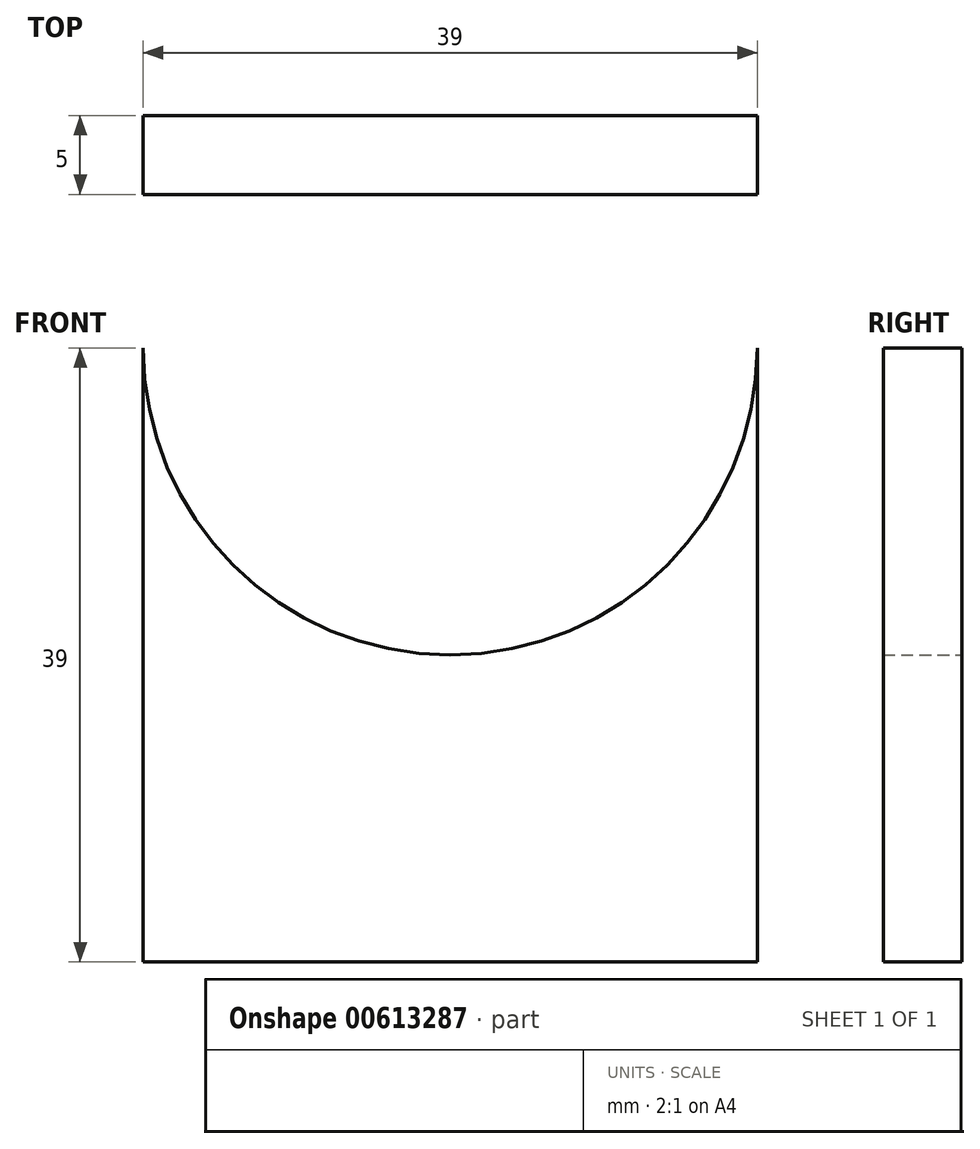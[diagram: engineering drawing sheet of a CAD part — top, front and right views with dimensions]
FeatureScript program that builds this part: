
annotation { "Feature Type Name" : "Feature", "Feature Type Description" : "" }
export const myFeature = defineFeature(function(context is Context, id is Id, definition is map)
    precondition{}
    {
        {
            var Q0;
            Q0=qCreatedBy(makeId("Front.planeOp"),FACE);
            var sketch = newSketch(context, id + "F0", { "sketchPlane" : qUnion([Q0])});
            skLineSegment(sketch, "E0.bottom", {"start": v(-13.94, 0) * mm, "end": v(25.06, 0) * mm});
            skLineSegment(sketch, "E0.top", {"start": v(-13.94, -39) * mm, "end": v(25.06, -39) * mm});
            skLineSegment(sketch, "E0.left", {"start": v(-13.94, 0) * mm, "end": v(-13.94, -39) * mm});
            skLineSegment(sketch, "E0.right", {"start": v(25.06, 0) * mm, "end": v(25.06, -39) * mm});
            skCircle(sketch, "E1", {"center": v(5.56, 0) * mm, "radius": 19.5 * mm});
            skLineSegment(sketch, "E2.bottom", {"start": v(25.06, -28.52) * mm, "end": v(-13.94, -28.52) * mm});
            skLineSegment(sketch, "E2.top", {"start": v(25.06, -39) * mm, "end": v(-13.94, -39) * mm});
            skLineSegment(sketch, "E2.left", {"start": v(25.06, -28.52) * mm, "end": v(25.06, -39) * mm});
            skLineSegment(sketch, "E2.right", {"start": v(-13.94, -28.52) * mm, "end": v(-13.94, -39) * mm});
            skSolve(sketch);
        }
        {
            var Q0;
            {var subQ0=sQuery(id+"F0.wireOp",EDGE,"E0.left");Q0=makeQuery(id+"F0.imprint","IMPRINT",FACE,{"disambiguationData":[TD([[makeQuery(id+"F0.imprint","IMPRINT",EDGE,{"derivedFrom":subQ0}),1.0]])]});}
            extrude(context, id + "F1", {"entities" : qUnion([Q0]), "depth" : 5 * mm, "offsetDistance" : 25 * mm});
        }
    });
